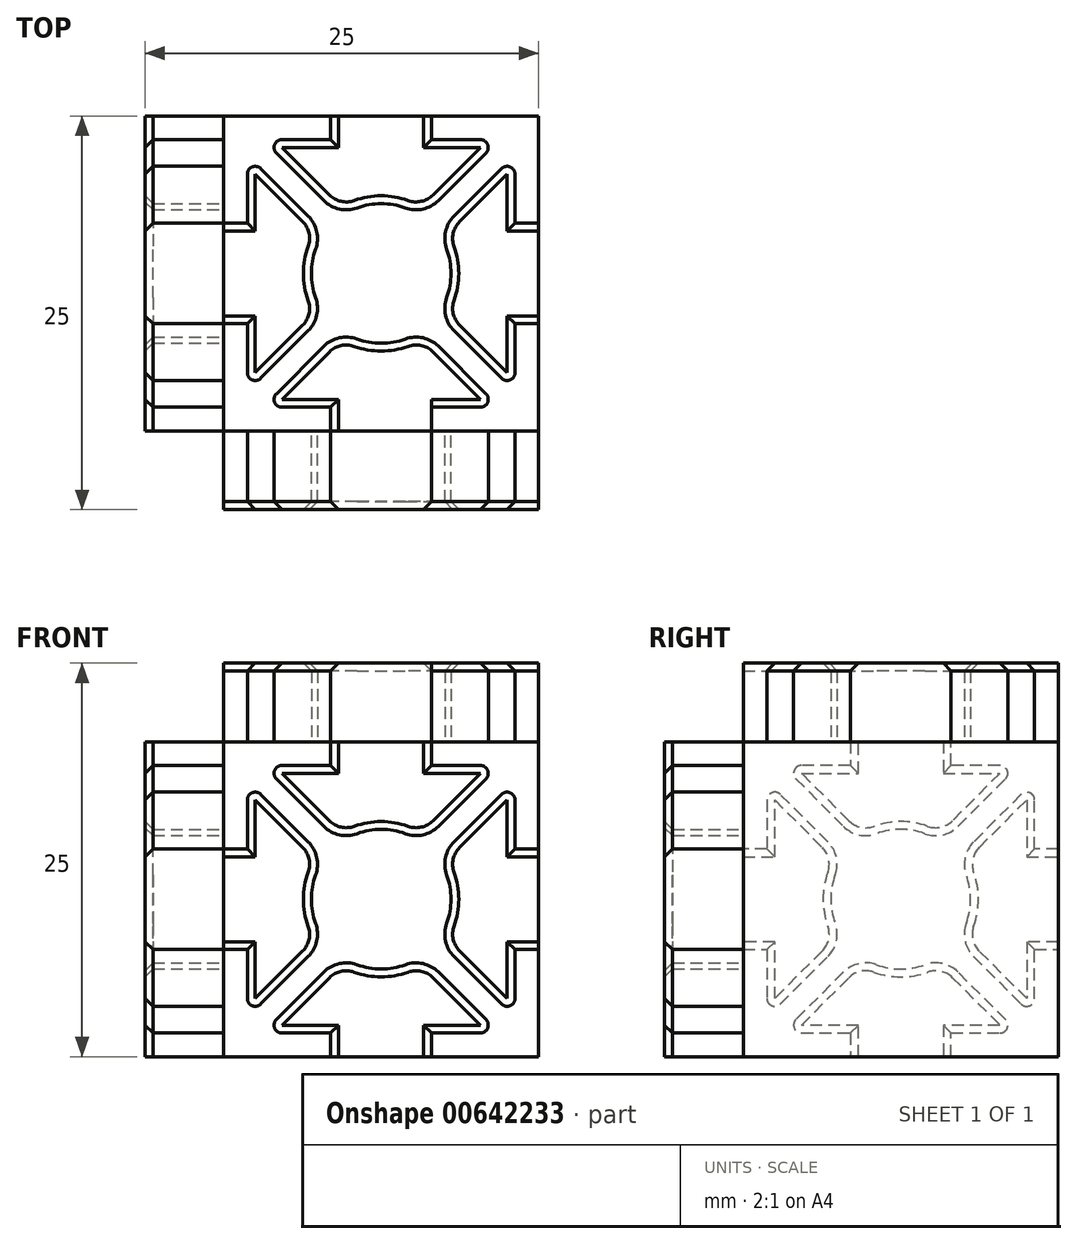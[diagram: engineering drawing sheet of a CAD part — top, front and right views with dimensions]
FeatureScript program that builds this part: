
annotation { "Feature Type Name" : "Feature", "Feature Type Description" : "" }
export const myFeature = defineFeature(function(context is Context, id is Id, definition is map)
    precondition{}
    {
        {
            var Q0;
            Q0=qCreatedBy(makeId("Top.planeOp"),FACE);
            var sketch = newSketch(context, id + "F0", { "sketchPlane" : qUnion([Q0])});
            skCircle(sketch, "E0", {"center": v(10, 10) * mm, "radius": 2.5 * mm});
            skLineSegment(sketch, "E1", {"start": v(0, 0) * mm, "end": v(10, 10) * mm, "construction": true});
            skLineSegment(sketch, "E2", {"start": v(1.5, 2.49) * mm, "end": v(1.5, 6.8) * mm});
            skLineSegment(sketch, "E3", {"start": v(1.5, 6.8) * mm, "end": v(0, 6.8) * mm});
            skLineSegment(sketch, "E4", {"start": v(0, 6.8) * mm, "end": v(0, 0) * mm});
            skLineSegment(sketch, "E5", {"start": v(7.39, 6.4) * mm, "end": v(2.49, 1.5) * mm});
            skLineSegment(sketch, "E6", {"start": v(2.49, 1.5) * mm, "end": v(6.8, 1.5) * mm});
            skLineSegment(sketch, "E7", {"start": v(6.8, 1.5) * mm, "end": v(6.8, 0) * mm});
            skLineSegment(sketch, "E8", {"start": v(6.8, 0) * mm, "end": v(0, 0) * mm});
            skLineSegment(sketch, "E9", {"start": v(10, 10) * mm, "end": v(20, 20) * mm, "construction": true});
            skLineSegment(sketch, "E10", {"start": v(10, 10) * mm, "end": v(0, 20) * mm, "construction": true});
            skLineSegment(sketch, "E11", {"start": v(10, 10) * mm, "end": v(20, 0) * mm, "construction": true});
            skLineSegment(sketch, "E12", {"start": v(1.5, 17.51) * mm, "end": v(6.4, 12.61) * mm});
            skLineSegment(sketch, "E13", {"start": v(1.5, 17.51) * mm, "end": v(1.5, 13.2) * mm});
            skLineSegment(sketch, "E14", {"start": v(1.5, 13.2) * mm, "end": v(0, 13.2) * mm});
            skLineSegment(sketch, "E15", {"start": v(0, 13.2) * mm, "end": v(0, 20) * mm});
            skLineSegment(sketch, "E16", {"start": v(7.39, 13.6) * mm, "end": v(2.49, 18.5) * mm});
            skLineSegment(sketch, "E17", {"start": v(2.49, 18.5) * mm, "end": v(6.8, 18.5) * mm});
            skLineSegment(sketch, "E18", {"start": v(6.8, 18.5) * mm, "end": v(6.8, 20) * mm});
            skLineSegment(sketch, "E19", {"start": v(6.8, 20) * mm, "end": v(0, 20) * mm});
            skLineSegment(sketch, "E20", {"start": v(12.61, 13.6) * mm, "end": v(17.51, 18.5) * mm});
            skLineSegment(sketch, "E21", {"start": v(17.51, 18.5) * mm, "end": v(13.2, 18.5) * mm});
            skLineSegment(sketch, "E22", {"start": v(13.2, 18.5) * mm, "end": v(13.2, 20) * mm});
            skLineSegment(sketch, "E23", {"start": v(13.2, 20) * mm, "end": v(20, 20) * mm});
            skLineSegment(sketch, "E24", {"start": v(13.6, 12.61) * mm, "end": v(18.5, 17.51) * mm});
            skLineSegment(sketch, "E25", {"start": v(18.5, 17.51) * mm, "end": v(18.5, 13.2) * mm});
            skLineSegment(sketch, "E26", {"start": v(18.5, 13.2) * mm, "end": v(20, 13.2) * mm});
            skLineSegment(sketch, "E27", {"start": v(20, 13.2) * mm, "end": v(20, 20) * mm});
            skLineSegment(sketch, "E28", {"start": v(18.5, 2.49) * mm, "end": v(18.5, 6.8) * mm});
            skLineSegment(sketch, "E29", {"start": v(18.5, 6.8) * mm, "end": v(20, 6.8) * mm});
            skLineSegment(sketch, "E30", {"start": v(20, 6.8) * mm, "end": v(20, 0) * mm});
            skLineSegment(sketch, "E31", {"start": v(12.61, 6.4) * mm, "end": v(17.51, 1.5) * mm});
            skLineSegment(sketch, "E32", {"start": v(17.51, 1.5) * mm, "end": v(13.2, 1.5) * mm});
            skLineSegment(sketch, "E33", {"start": v(13.2, 1.5) * mm, "end": v(13.2, 0) * mm});
            skLineSegment(sketch, "E34", {"start": v(13.2, 0) * mm, "end": v(20, 0) * mm});
            skLineSegment(sketch, "E35", {"start": v(10, 10) * mm, "end": v(10, 0) * mm, "construction": true});
            skLineSegment(sketch, "E36", {"start": v(10, 10) * mm, "end": v(18.77, 10) * mm, "construction": true});
            skLineSegment(sketch, "E37", {"start": v(10, 10) * mm, "end": v(10, 20.74) * mm, "construction": true});
            skLineSegment(sketch, "E38", {"start": v(10, 10) * mm, "end": v(0, 10) * mm, "construction": true});
            skLineSegment(sketch, "E39.bottom", {"start": v(0, 0) * mm, "end": v(20, 0) * mm, "construction": true});
            skLineSegment(sketch, "E39.top", {"start": v(0, 20) * mm, "end": v(20, 20) * mm, "construction": true});
            skLineSegment(sketch, "E39.left", {"start": v(0, 0) * mm, "end": v(0, 20) * mm, "construction": true});
            skLineSegment(sketch, "E39.right", {"start": v(20, 0) * mm, "end": v(20, 20) * mm, "construction": true});
            skLineSegment(sketch, "E40", {"start": v(18.5, 2.49) * mm, "end": v(13.6, 7.39) * mm});
            skLineSegment(sketch, "E41", {"start": v(1.5, 2.49) * mm, "end": v(6.4, 7.39) * mm});
            skLineSegment(sketch, "E42", {"start": v(20, 13.2) * mm, "end": v(20, 6.8) * mm});
            skLineSegment(sketch, "E43", {"start": v(6.8, 20) * mm, "end": v(13.2, 20) * mm});
            skLineSegment(sketch, "E44", {"start": v(0, 13.2) * mm, "end": v(0, 6.8) * mm});
            skLineSegment(sketch, "E45", {"start": v(6.8, 0) * mm, "end": v(13.2, 0) * mm});
            skArc(sketch, "E46", {"start": v(12.61, 13.6) * mm, "mid": v(10, 14.43) * mm, "end": v(7.39, 13.6) * mm});
            skArc(sketch, "E47", {"start": v(6.4, 12.61) * mm, "mid": v(5.57, 10) * mm, "end": v(6.4, 7.39) * mm});
            skArc(sketch, "E48", {"start": v(13.6, 7.39) * mm, "mid": v(14.43, 10) * mm, "end": v(13.6, 12.61) * mm});
            skArc(sketch, "E49", {"start": v(7.39, 6.4) * mm, "mid": v(10, 5.57) * mm, "end": v(12.61, 6.4) * mm});
            skSolve(sketch);
        }
        {
            var Q0;
            Q0=makeQuery(id+"F0.imprint","IMPRINT",FACE,{"disambiguationData":[TD([[makeQuery(id+"F0.imprint","IMPRINT",EDGE,{"derivedFrom":sQuery(id+"F0.wireOp",EDGE,"E16")}),-1.0]])]});
            var Q1;
            Q1=makeQuery(id+"F0.imprint","IMPRINT",FACE,{"disambiguationData":[TD([[makeQuery(id+"F0.imprint","IMPRINT",EDGE,{"derivedFrom":sQuery(id+"F0.wireOp",EDGE,"E24")}),-1.0]])]});
            var Q2;
            Q2=makeQuery(id+"F0.imprint","IMPRINT",FACE,{"disambiguationData":[TD([[makeQuery(id+"F0.imprint","IMPRINT",EDGE,{"derivedFrom":sQuery(id+"F0.wireOp",EDGE,"E5")}),1.0]])]});
            var Q3;
            Q3=makeQuery(id+"F0.imprint","IMPRINT",FACE,{"disambiguationData":[TD([[makeQuery(id+"F0.imprint","IMPRINT",EDGE,{"derivedFrom":sQuery(id+"F0.wireOp",EDGE,"E2")}),-1.0]])]});
            extrude(context, id + "F1", {"entities" : qUnion([Q0, Q1, Q2, Q3]), "depth" : 5 * mm, "offsetDistance" : 25 * mm});
        }
        {
            var Q0;
            Q0=qCreatedBy(makeId("Right.planeOp"),FACE);
            var sketch = newSketch(context, id + "F2", { "sketchPlane" : qUnion([Q0])});
            skCircle(sketch, "E50", {"center": v(10, -10) * mm, "radius": 2.5 * mm});
            skLineSegment(sketch, "E51", {"start": v(0, -20) * mm, "end": v(10, -10) * mm, "construction": true});
            skLineSegment(sketch, "E52", {"start": v(1.5, -17.51) * mm, "end": v(1.5, -13.2) * mm});
            skLineSegment(sketch, "E53", {"start": v(1.5, -13.2) * mm, "end": v(0, -13.2) * mm});
            skLineSegment(sketch, "E54", {"start": v(7.39, -13.6) * mm, "end": v(2.49, -18.5) * mm});
            skLineSegment(sketch, "E55", {"start": v(2.49, -18.5) * mm, "end": v(6.8, -18.5) * mm});
            skLineSegment(sketch, "E56", {"start": v(6.8, -18.5) * mm, "end": v(6.8, -20) * mm});
            skLineSegment(sketch, "E57", {"start": v(10, -10) * mm, "end": v(20, 0) * mm, "construction": true});
            skLineSegment(sketch, "E58", {"start": v(10, -10) * mm, "end": v(0, 0) * mm, "construction": true});
            skLineSegment(sketch, "E59", {"start": v(10, -10) * mm, "end": v(20, -20) * mm, "construction": true});
            skLineSegment(sketch, "E60", {"start": v(1.5, -2.49) * mm, "end": v(6.4, -7.39) * mm});
            skLineSegment(sketch, "E61", {"start": v(1.5, -2.49) * mm, "end": v(1.5, -6.8) * mm});
            skLineSegment(sketch, "E62", {"start": v(1.5, -6.8) * mm, "end": v(0, -6.8) * mm});
            skLineSegment(sketch, "E63", {"start": v(7.39, -6.4) * mm, "end": v(2.49, -1.5) * mm});
            skLineSegment(sketch, "E64", {"start": v(2.49, -1.5) * mm, "end": v(6.8, -1.5) * mm});
            skLineSegment(sketch, "E65", {"start": v(6.8, -1.5) * mm, "end": v(6.8, 0) * mm});
            skLineSegment(sketch, "E66", {"start": v(12.61, -6.4) * mm, "end": v(17.51, -1.5) * mm});
            skLineSegment(sketch, "E67", {"start": v(17.51, -1.5) * mm, "end": v(13.2, -1.5) * mm});
            skLineSegment(sketch, "E68", {"start": v(13.2, -1.5) * mm, "end": v(13.2, 0) * mm});
            skLineSegment(sketch, "E69", {"start": v(13.6, -7.39) * mm, "end": v(18.5, -2.49) * mm});
            skLineSegment(sketch, "E70", {"start": v(18.5, -2.49) * mm, "end": v(18.5, -6.8) * mm});
            skLineSegment(sketch, "E71", {"start": v(18.5, -6.8) * mm, "end": v(20, -6.8) * mm});
            skLineSegment(sketch, "E72", {"start": v(18.5, -17.51) * mm, "end": v(18.5, -13.2) * mm});
            skLineSegment(sketch, "E73", {"start": v(18.5, -13.2) * mm, "end": v(20, -13.2) * mm});
            skLineSegment(sketch, "E74", {"start": v(12.61, -13.6) * mm, "end": v(17.51, -18.5) * mm});
            skLineSegment(sketch, "E75", {"start": v(17.51, -18.5) * mm, "end": v(13.2, -18.5) * mm});
            skLineSegment(sketch, "E76", {"start": v(13.2, -18.5) * mm, "end": v(13.2, -20) * mm});
            skLineSegment(sketch, "E77", {"start": v(18.5, -17.51) * mm, "end": v(13.6, -12.61) * mm});
            skLineSegment(sketch, "E78", {"start": v(1.5, -17.51) * mm, "end": v(6.4, -12.61) * mm});
            skLineSegment(sketch, "E79", {"start": v(20, -6.8) * mm, "end": v(20, -13.2) * mm});
            skLineSegment(sketch, "E80", {"start": v(6.8, 0) * mm, "end": v(13.2, 0) * mm});
            skLineSegment(sketch, "E81", {"start": v(0, -6.8) * mm, "end": v(0, -13.2) * mm});
            skLineSegment(sketch, "E82", {"start": v(6.8, -20) * mm, "end": v(13.2, -20) * mm});
            skArc(sketch, "E83", {"start": v(12.61, -6.4) * mm, "mid": v(10, -5.57) * mm, "end": v(7.39, -6.4) * mm});
            skArc(sketch, "E84", {"start": v(6.4, -7.39) * mm, "mid": v(5.57, -10) * mm, "end": v(6.4, -12.61) * mm});
            skArc(sketch, "E85", {"start": v(13.6, -12.61) * mm, "mid": v(14.43, -10) * mm, "end": v(13.6, -7.39) * mm});
            skArc(sketch, "E86", {"start": v(7.39, -13.6) * mm, "mid": v(10, -14.43) * mm, "end": v(12.61, -13.6) * mm});
            skLineSegment(sketch, "E87.bottom", {"start": v(20, 0) * mm, "end": v(0, 0) * mm, "construction": true});
            skLineSegment(sketch, "E87.top", {"start": v(20, -20) * mm, "end": v(0, -20) * mm, "construction": true});
            skLineSegment(sketch, "E87.left", {"start": v(20, 0) * mm, "end": v(20, -20) * mm, "construction": true});
            skLineSegment(sketch, "E87.right", {"start": v(0, 0) * mm, "end": v(0, -20) * mm, "construction": true});
            skSolve(sketch);
        }
        {
            var Q0;
            Q0=makeQuery(id+"F2.imprint","IMPRINT",FACE,{"disambiguationData":[TD([[makeQuery(id+"F2.imprint","IMPRINT",EDGE,{"derivedFrom":sQuery(id+"F2.wireOp",EDGE,"E63")}),-1.0]])]});
            var Q1;
            Q1=makeQuery(id+"F2.imprint","IMPRINT",FACE,{"disambiguationData":[TD([[makeQuery(id+"F2.imprint","IMPRINT",EDGE,{"derivedFrom":sQuery(id+"F2.wireOp",EDGE,"E69")}),-1.0]])]});
            var Q2;
            Q2=makeQuery(id+"F2.imprint","IMPRINT",FACE,{"disambiguationData":[TD([[makeQuery(id+"F2.imprint","IMPRINT",EDGE,{"derivedFrom":sQuery(id+"F2.wireOp",EDGE,"E54")}),1.0]])]});
            var Q3;
            Q3=makeQuery(id+"F2.imprint","IMPRINT",FACE,{"disambiguationData":[TD([[makeQuery(id+"F2.imprint","IMPRINT",EDGE,{"derivedFrom":sQuery(id+"F2.wireOp",EDGE,"E52")}),-1.0]])]});
            extrude(context, id + "F3", {"entities" : qUnion([Q0, Q1, Q2, Q3]), "operationType" : NewBodyOperationType.ADD, "oppositeDirection" : true, "depth" : 5 * mm, "offsetDistance" : 25 * mm});
        }
        {
            var Q0;
            Q0=qCreatedBy(makeId("Front.planeOp"),FACE);
            var sketch = newSketch(context, id + "F4", { "sketchPlane" : qUnion([Q0])});
            skCircle(sketch, "E88", {"center": v(10, -10) * mm, "radius": 2.5 * mm});
            skLineSegment(sketch, "E89", {"start": v(0, -20) * mm, "end": v(10, -10) * mm, "construction": true});
            skLineSegment(sketch, "E90", {"start": v(1.5, -17.51) * mm, "end": v(1.5, -13.2) * mm});
            skLineSegment(sketch, "E91", {"start": v(1.5, -13.2) * mm, "end": v(0, -13.2) * mm});
            skLineSegment(sketch, "E92", {"start": v(7.39, -13.6) * mm, "end": v(2.49, -18.5) * mm});
            skLineSegment(sketch, "E93", {"start": v(2.49, -18.5) * mm, "end": v(6.8, -18.5) * mm});
            skLineSegment(sketch, "E94", {"start": v(6.8, -18.5) * mm, "end": v(6.8, -20) * mm});
            skLineSegment(sketch, "E95", {"start": v(10, -10) * mm, "end": v(20, 0) * mm, "construction": true});
            skLineSegment(sketch, "E96", {"start": v(10, -10) * mm, "end": v(0, 0) * mm, "construction": true});
            skLineSegment(sketch, "E97", {"start": v(10, -10) * mm, "end": v(20, -20) * mm, "construction": true});
            skLineSegment(sketch, "E98", {"start": v(1.5, -2.49) * mm, "end": v(6.4, -7.39) * mm});
            skLineSegment(sketch, "E99", {"start": v(1.5, -2.49) * mm, "end": v(1.5, -6.8) * mm});
            skLineSegment(sketch, "E100", {"start": v(1.5, -6.8) * mm, "end": v(0, -6.8) * mm});
            skLineSegment(sketch, "E101", {"start": v(7.39, -6.4) * mm, "end": v(2.49, -1.5) * mm});
            skLineSegment(sketch, "E102", {"start": v(2.49, -1.5) * mm, "end": v(6.8, -1.5) * mm});
            skLineSegment(sketch, "E103", {"start": v(6.8, -1.5) * mm, "end": v(6.8, 0) * mm});
            skLineSegment(sketch, "E104", {"start": v(12.61, -6.4) * mm, "end": v(17.51, -1.5) * mm});
            skLineSegment(sketch, "E105", {"start": v(17.51, -1.5) * mm, "end": v(13.2, -1.5) * mm});
            skLineSegment(sketch, "E106", {"start": v(13.2, -1.5) * mm, "end": v(13.2, 0) * mm});
            skLineSegment(sketch, "E107", {"start": v(13.6, -7.39) * mm, "end": v(18.5, -2.49) * mm});
            skLineSegment(sketch, "E108", {"start": v(18.5, -2.49) * mm, "end": v(18.5, -6.8) * mm});
            skLineSegment(sketch, "E109", {"start": v(18.5, -6.8) * mm, "end": v(20, -6.8) * mm});
            skLineSegment(sketch, "E110", {"start": v(18.5, -17.51) * mm, "end": v(18.5, -13.2) * mm});
            skLineSegment(sketch, "E111", {"start": v(18.5, -13.2) * mm, "end": v(20, -13.2) * mm});
            skLineSegment(sketch, "E112", {"start": v(12.61, -13.6) * mm, "end": v(17.51, -18.5) * mm});
            skLineSegment(sketch, "E113", {"start": v(17.51, -18.5) * mm, "end": v(13.2, -18.5) * mm});
            skLineSegment(sketch, "E114", {"start": v(13.2, -18.5) * mm, "end": v(13.2, -20) * mm});
            skLineSegment(sketch, "E115", {"start": v(18.5, -17.51) * mm, "end": v(13.6, -12.61) * mm});
            skLineSegment(sketch, "E116", {"start": v(1.5, -17.51) * mm, "end": v(6.4, -12.61) * mm});
            skLineSegment(sketch, "E117", {"start": v(20, -6.8) * mm, "end": v(20, -13.2) * mm});
            skLineSegment(sketch, "E118", {"start": v(6.8, 0) * mm, "end": v(13.2, 0) * mm});
            skLineSegment(sketch, "E119", {"start": v(0, -6.8) * mm, "end": v(0, -13.2) * mm});
            skLineSegment(sketch, "E120", {"start": v(6.8, -20) * mm, "end": v(13.2, -20) * mm});
            skArc(sketch, "E121", {"start": v(12.61, -6.4) * mm, "mid": v(10, -5.57) * mm, "end": v(7.39, -6.4) * mm});
            skArc(sketch, "E122", {"start": v(6.4, -7.39) * mm, "mid": v(5.57, -10) * mm, "end": v(6.4, -12.61) * mm});
            skArc(sketch, "E123", {"start": v(13.6, -12.61) * mm, "mid": v(14.43, -10) * mm, "end": v(13.6, -7.39) * mm});
            skArc(sketch, "E124", {"start": v(7.39, -13.6) * mm, "mid": v(10, -14.43) * mm, "end": v(12.61, -13.6) * mm});
            skLineSegment(sketch, "E125.bottom", {"start": v(0, 0) * mm, "end": v(20, 0) * mm, "construction": true});
            skLineSegment(sketch, "E125.top", {"start": v(0, -20) * mm, "end": v(20, -20) * mm, "construction": true});
            skLineSegment(sketch, "E125.left", {"start": v(0, 0) * mm, "end": v(0, -20) * mm, "construction": true});
            skLineSegment(sketch, "E125.right", {"start": v(20, 0) * mm, "end": v(20, -20) * mm, "construction": true});
            skSolve(sketch);
        }
        {
            var Q0;
            Q0=makeQuery(id+"F4.imprint","IMPRINT",FACE,{"disambiguationData":[TD([[makeQuery(id+"F4.imprint","IMPRINT",EDGE,{"derivedFrom":sQuery(id+"F4.wireOp",EDGE,"E101")}),-1.0]])]});
            var Q1;
            Q1=makeQuery(id+"F4.imprint","IMPRINT",FACE,{"disambiguationData":[TD([[makeQuery(id+"F4.imprint","IMPRINT",EDGE,{"derivedFrom":sQuery(id+"F4.wireOp",EDGE,"E107")}),-1.0]])]});
            var Q2;
            Q2=makeQuery(id+"F4.imprint","IMPRINT",FACE,{"disambiguationData":[TD([[makeQuery(id+"F4.imprint","IMPRINT",EDGE,{"derivedFrom":sQuery(id+"F4.wireOp",EDGE,"E92")}),1.0]])]});
            var Q3;
            Q3=makeQuery(id+"F4.imprint","IMPRINT",FACE,{"disambiguationData":[TD([[makeQuery(id+"F4.imprint","IMPRINT",EDGE,{"derivedFrom":sQuery(id+"F4.wireOp",EDGE,"E90")}),-1.0]])]});
            extrude(context, id + "F5", {"entities" : qUnion([Q0, Q1, Q2, Q3]), "operationType" : NewBodyOperationType.ADD, "depth" : 5 * mm, "offsetDistance" : 25 * mm});
        }
        {
            var Q0;
            Q0=makeQuery(id+"F0.imprint","IMPRINT",FACE,{"disambiguationData":[TD([[makeQuery(id+"F0.imprint","IMPRINT",EDGE,{"derivedFrom":sQuery(id+"F0.wireOp",EDGE,"E0")}),-1.0]])]});
            var sketch = newSketch(context, id + "F6", { "sketchPlane" : qUnion([Q0])});
            skLineSegment(sketch, "E126.bottom", {"start": v(0, 0) * mm, "end": v(20, 0) * mm});
            skLineSegment(sketch, "E126.top", {"start": v(0, 20) * mm, "end": v(20, 20) * mm});
            skLineSegment(sketch, "E126.left", {"start": v(0, 0) * mm, "end": v(0, 20) * mm});
            skLineSegment(sketch, "E126.right", {"start": v(20, 0) * mm, "end": v(20, 20) * mm});
            skSolve(sketch);
        }
        {
            var Q0;
            Q0=makeQuery(id+"F6.imprint","IMPRINT",FACE,{"disambiguationData":[TD([[makeQuery(id+"F6.imprint","IMPRINT",EDGE,{"derivedFrom":makeQuery(id+"F0.imprint","IMPRINT",EDGE,{"derivedFrom":sQuery(id+"F0.wireOp",EDGE,"E0")})}),-1.0]])]});
            var Q1;
            Q1=makeQuery(id+"F6.imprint","IMPRINT",FACE,{"disambiguationData":[TD([[makeQuery(id+"F6.imprint","IMPRINT",EDGE,{"derivedFrom":makeQuery(id+"F0.imprint","IMPRINT",EDGE,{"derivedFrom":sQuery(id+"F0.wireOp",EDGE,"E24")})}),-1.0]])]});
            var Q2;
            Q2=makeQuery(id+"F6.imprint","IMPRINT",FACE,{"disambiguationData":[TD([[makeQuery(id+"F6.imprint","IMPRINT",EDGE,{"derivedFrom":makeQuery(id+"F0.imprint","IMPRINT",EDGE,{"derivedFrom":sQuery(id+"F0.wireOp",EDGE,"E16")})}),-1.0]])]});
            var Q3;
            Q3=makeQuery(id+"F6.imprint","IMPRINT",FACE,{"disambiguationData":[TD([[makeQuery(id+"F6.imprint","IMPRINT",EDGE,{"derivedFrom":makeQuery(id+"F0.imprint","IMPRINT",EDGE,{"derivedFrom":sQuery(id+"F0.wireOp",EDGE,"E2")})}),-1.0]])]});
            var Q4;
            Q4=makeQuery(id+"F6.imprint","IMPRINT",FACE,{"disambiguationData":[TD([[makeQuery(id+"F6.imprint","IMPRINT",EDGE,{"derivedFrom":makeQuery(id+"F0.imprint","IMPRINT",EDGE,{"derivedFrom":sQuery(id+"F0.wireOp",EDGE,"E5")})}),1.0]])]});
            var Q5;
            Q5=makeQuery(id+"F6.imprint","IMPRINT",FACE,{"disambiguationData":[TD([[makeQuery(id+"F6.imprint","IMPRINT",EDGE,{"derivedFrom":makeQuery(id+"F0.imprint","IMPRINT",EDGE,{"derivedFrom":sQuery(id+"F0.wireOp",EDGE,"E0")})}),1.0]])]});
            extrude(context, id + "F7", {"entities" : qUnion([Q0, Q1, Q2, Q3, Q4, Q5]), "oppositeDirection" : true, "depth" : 20 * mm, "offsetDistance" : 25 * mm});
        }
        {
            var Q0;
            Q0=makeQuery(id+"F5.opExtrude","SWEPT_EDGE",EDGE,{"disambiguationData":[OSD([sQuery(id+"F4.wireOp",EDGE,"E107"),sQuery(id+"F4.wireOp",EDGE,"E108")])]});
            var Q1;
            Q1=makeQuery(id+"F5.opExtrude","SWEPT_EDGE",EDGE,{"disambiguationData":[OSD([sQuery(id+"F4.wireOp",EDGE,"E104"),sQuery(id+"F4.wireOp",EDGE,"E105")])]});
            var Q2;
            Q2=makeQuery(id+"F5.opExtrude","SWEPT_EDGE",EDGE,{"disambiguationData":[OSD([sQuery(id+"F4.wireOp",EDGE,"E110"),sQuery(id+"F4.wireOp",EDGE,"E115")])]});
            var Q3;
            Q3=makeQuery(id+"F5.opExtrude","SWEPT_EDGE",EDGE,{"disambiguationData":[OSD([sQuery(id+"F4.wireOp",EDGE,"E112"),sQuery(id+"F4.wireOp",EDGE,"E113")])]});
            var Q4;
            Q4=makeQuery(id+"F5.opExtrude","SWEPT_EDGE",EDGE,{"disambiguationData":[OSD([sQuery(id+"F4.wireOp",EDGE,"E92"),sQuery(id+"F4.wireOp",EDGE,"E93")])]});
            var Q5;
            Q5=makeQuery(id+"F5.opExtrude","SWEPT_EDGE",EDGE,{"disambiguationData":[OSD([sQuery(id+"F4.wireOp",EDGE,"E90"),sQuery(id+"F4.wireOp",EDGE,"E116")])]});
            var Q6;
            Q6=makeQuery(id+"F5.opExtrude","SWEPT_EDGE",EDGE,{"disambiguationData":[OSD([sQuery(id+"F4.wireOp",EDGE,"E98"),sQuery(id+"F4.wireOp",EDGE,"E99")])]});
            var Q7;
            Q7=makeQuery(id+"F5.opExtrude","SWEPT_EDGE",EDGE,{"disambiguationData":[OSD([sQuery(id+"F4.wireOp",EDGE,"E101"),sQuery(id+"F4.wireOp",EDGE,"E102")])]});
            var Q8;
            Q8=makeQuery(id+"F1.opExtrude","SWEPT_EDGE",EDGE,{"disambiguationData":[OSD([sQuery(id+"F0.wireOp",EDGE,"E5"),sQuery(id+"F0.wireOp",EDGE,"E6")])]});
            var Q9;
            Q9=makeQuery(id+"F1.opExtrude","SWEPT_EDGE",EDGE,{"disambiguationData":[OSD([sQuery(id+"F0.wireOp",EDGE,"E2"),sQuery(id+"F0.wireOp",EDGE,"E41")])]});
            var Q10;
            Q10=makeQuery(id+"F1.opExtrude","SWEPT_EDGE",EDGE,{"disambiguationData":[OSD([sQuery(id+"F0.wireOp",EDGE,"E31"),sQuery(id+"F0.wireOp",EDGE,"E32")])]});
            var Q11;
            Q11=makeQuery(id+"F1.opExtrude","SWEPT_EDGE",EDGE,{"disambiguationData":[OSD([sQuery(id+"F0.wireOp",EDGE,"E28"),sQuery(id+"F0.wireOp",EDGE,"E40")])]});
            var Q12;
            Q12=makeQuery(id+"F1.opExtrude","SWEPT_EDGE",EDGE,{"disambiguationData":[OSD([sQuery(id+"F0.wireOp",EDGE,"E24"),sQuery(id+"F0.wireOp",EDGE,"E25")])]});
            var Q13;
            Q13=makeQuery(id+"F1.opExtrude","SWEPT_EDGE",EDGE,{"disambiguationData":[OSD([sQuery(id+"F0.wireOp",EDGE,"E20"),sQuery(id+"F0.wireOp",EDGE,"E21")])]});
            var Q14;
            Q14=makeQuery(id+"F1.opExtrude","SWEPT_EDGE",EDGE,{"disambiguationData":[OSD([sQuery(id+"F0.wireOp",EDGE,"E16"),sQuery(id+"F0.wireOp",EDGE,"E17")])]});
            var Q15;
            Q15=makeQuery(id+"F1.opExtrude","SWEPT_EDGE",EDGE,{"disambiguationData":[OSD([sQuery(id+"F0.wireOp",EDGE,"E12"),sQuery(id+"F0.wireOp",EDGE,"E13")])]});
            var Q16;
            Q16=makeQuery(id+"F3.opExtrude","SWEPT_EDGE",EDGE,{"disambiguationData":[OSD([sQuery(id+"F2.wireOp",EDGE,"E66"),sQuery(id+"F2.wireOp",EDGE,"E67")])]});
            var Q17;
            Q17=makeQuery(id+"F3.opExtrude","SWEPT_EDGE",EDGE,{"disambiguationData":[OSD([sQuery(id+"F2.wireOp",EDGE,"E69"),sQuery(id+"F2.wireOp",EDGE,"E70")])]});
            var Q18;
            Q18=makeQuery(id+"F3.opExtrude","SWEPT_EDGE",EDGE,{"disambiguationData":[OSD([sQuery(id+"F2.wireOp",EDGE,"E63"),sQuery(id+"F2.wireOp",EDGE,"E64")])]});
            var Q19;
            Q19=makeQuery(id+"F3.opExtrude","SWEPT_EDGE",EDGE,{"disambiguationData":[OSD([sQuery(id+"F2.wireOp",EDGE,"E60"),sQuery(id+"F2.wireOp",EDGE,"E61")])]});
            var Q20;
            Q20=makeQuery(id+"F3.opExtrude","SWEPT_EDGE",EDGE,{"disambiguationData":[OSD([sQuery(id+"F2.wireOp",EDGE,"E52"),sQuery(id+"F2.wireOp",EDGE,"E78")])]});
            var Q21;
            Q21=makeQuery(id+"F3.opExtrude","SWEPT_EDGE",EDGE,{"disambiguationData":[OSD([sQuery(id+"F2.wireOp",EDGE,"E54"),sQuery(id+"F2.wireOp",EDGE,"E55")])]});
            var Q22;
            Q22=makeQuery(id+"F3.opExtrude","SWEPT_EDGE",EDGE,{"disambiguationData":[OSD([sQuery(id+"F2.wireOp",EDGE,"E74"),sQuery(id+"F2.wireOp",EDGE,"E75")])]});
            var Q23;
            Q23=makeQuery(id+"F3.opExtrude","SWEPT_EDGE",EDGE,{"disambiguationData":[OSD([sQuery(id+"F2.wireOp",EDGE,"E72"),sQuery(id+"F2.wireOp",EDGE,"E77")])]});
            fillet(context, id + "F8", {"entities" : qUnion([Q0, Q1, Q2, Q3, Q4, Q5, Q6, Q7, Q8, Q9, Q10, Q11, Q12, Q13, Q14, Q15, Q16, Q17, Q18, Q19, Q20, Q21, Q22, Q23]), "radius" : 0.5 * mm, "tangentPropagation" : true, "allowEdgeOverflow" : false});
        }
        {
            var Q0;
            Q0=makeQuery(id+"F3.opExtrude","SWEPT_EDGE",EDGE,{"disambiguationData":[OSD([sQuery(id+"F2.wireOp",EDGE,"E69"),sQuery(id+"F2.wireOp",EDGE,"E85")])]});
            var Q1;
            Q1=makeQuery(id+"F3.opExtrude","SWEPT_EDGE",EDGE,{"disambiguationData":[OSD([sQuery(id+"F2.wireOp",EDGE,"E77"),sQuery(id+"F2.wireOp",EDGE,"E85")])]});
            var Q2;
            Q2=makeQuery(id+"F3.opExtrude","SWEPT_EDGE",EDGE,{"disambiguationData":[OSD([sQuery(id+"F2.wireOp",EDGE,"E66"),sQuery(id+"F2.wireOp",EDGE,"E83")])]});
            var Q3;
            Q3=makeQuery(id+"F3.opExtrude","SWEPT_EDGE",EDGE,{"disambiguationData":[OSD([sQuery(id+"F2.wireOp",EDGE,"E63"),sQuery(id+"F2.wireOp",EDGE,"E83")])]});
            var Q4;
            Q4=makeQuery(id+"F3.opExtrude","SWEPT_EDGE",EDGE,{"disambiguationData":[OSD([sQuery(id+"F2.wireOp",EDGE,"E78"),sQuery(id+"F2.wireOp",EDGE,"E84")])]});
            var Q5;
            Q5=makeQuery(id+"F3.opExtrude","SWEPT_EDGE",EDGE,{"disambiguationData":[OSD([sQuery(id+"F2.wireOp",EDGE,"E60"),sQuery(id+"F2.wireOp",EDGE,"E84")])]});
            var Q6;
            Q6=makeQuery(id+"F3.opExtrude","SWEPT_EDGE",EDGE,{"disambiguationData":[OSD([sQuery(id+"F2.wireOp",EDGE,"E74"),sQuery(id+"F2.wireOp",EDGE,"E86")])]});
            var Q7;
            Q7=makeQuery(id+"F3.opExtrude","SWEPT_EDGE",EDGE,{"disambiguationData":[OSD([sQuery(id+"F2.wireOp",EDGE,"E54"),sQuery(id+"F2.wireOp",EDGE,"E86")])]});
            var Q8;
            Q8=makeQuery(id+"F5.opExtrude","SWEPT_EDGE",EDGE,{"disambiguationData":[OSD([sQuery(id+"F4.wireOp",EDGE,"E98"),sQuery(id+"F4.wireOp",EDGE,"E122")])]});
            var Q9;
            Q9=makeQuery(id+"F5.opExtrude","SWEPT_EDGE",EDGE,{"disambiguationData":[OSD([sQuery(id+"F4.wireOp",EDGE,"E116"),sQuery(id+"F4.wireOp",EDGE,"E122")])]});
            var Q10;
            Q10=makeQuery(id+"F5.opExtrude","SWEPT_EDGE",EDGE,{"disambiguationData":[OSD([sQuery(id+"F4.wireOp",EDGE,"E92"),sQuery(id+"F4.wireOp",EDGE,"E124")])]});
            var Q11;
            Q11=makeQuery(id+"F5.opExtrude","SWEPT_EDGE",EDGE,{"disambiguationData":[OSD([sQuery(id+"F4.wireOp",EDGE,"E112"),sQuery(id+"F4.wireOp",EDGE,"E124")])]});
            var Q12;
            Q12=makeQuery(id+"F5.opExtrude","SWEPT_EDGE",EDGE,{"disambiguationData":[OSD([sQuery(id+"F4.wireOp",EDGE,"E115"),sQuery(id+"F4.wireOp",EDGE,"E123")])]});
            var Q13;
            Q13=makeQuery(id+"F5.opExtrude","SWEPT_EDGE",EDGE,{"disambiguationData":[OSD([sQuery(id+"F4.wireOp",EDGE,"E101"),sQuery(id+"F4.wireOp",EDGE,"E121")])]});
            var Q14;
            Q14=makeQuery(id+"F5.opExtrude","SWEPT_EDGE",EDGE,{"disambiguationData":[OSD([sQuery(id+"F4.wireOp",EDGE,"E104"),sQuery(id+"F4.wireOp",EDGE,"E121")])]});
            var Q15;
            Q15=makeQuery(id+"F5.opExtrude","SWEPT_EDGE",EDGE,{"disambiguationData":[OSD([sQuery(id+"F4.wireOp",EDGE,"E107"),sQuery(id+"F4.wireOp",EDGE,"E123")])]});
            var Q16;
            Q16=makeQuery(id+"F1.opExtrude","SWEPT_EDGE",EDGE,{"disambiguationData":[OSD([sQuery(id+"F0.wireOp",EDGE,"E12"),sQuery(id+"F0.wireOp",EDGE,"E47")])]});
            var Q17;
            Q17=makeQuery(id+"F1.opExtrude","SWEPT_EDGE",EDGE,{"disambiguationData":[OSD([sQuery(id+"F0.wireOp",EDGE,"E41"),sQuery(id+"F0.wireOp",EDGE,"E47")])]});
            var Q18;
            Q18=makeQuery(id+"F1.opExtrude","SWEPT_EDGE",EDGE,{"disambiguationData":[OSD([sQuery(id+"F0.wireOp",EDGE,"E5"),sQuery(id+"F0.wireOp",EDGE,"E49")])]});
            var Q19;
            Q19=makeQuery(id+"F1.opExtrude","SWEPT_EDGE",EDGE,{"disambiguationData":[OSD([sQuery(id+"F0.wireOp",EDGE,"E40"),sQuery(id+"F0.wireOp",EDGE,"E48")])]});
            var Q20;
            Q20=makeQuery(id+"F1.opExtrude","SWEPT_EDGE",EDGE,{"disambiguationData":[OSD([sQuery(id+"F0.wireOp",EDGE,"E31"),sQuery(id+"F0.wireOp",EDGE,"E49")])]});
            var Q21;
            Q21=makeQuery(id+"F1.opExtrude","SWEPT_EDGE",EDGE,{"disambiguationData":[OSD([sQuery(id+"F0.wireOp",EDGE,"E20"),sQuery(id+"F0.wireOp",EDGE,"E46")])]});
            var Q22;
            Q22=makeQuery(id+"F1.opExtrude","SWEPT_EDGE",EDGE,{"disambiguationData":[OSD([sQuery(id+"F0.wireOp",EDGE,"E16"),sQuery(id+"F0.wireOp",EDGE,"E46")])]});
            var Q23;
            Q23=makeQuery(id+"F1.opExtrude","SWEPT_EDGE",EDGE,{"disambiguationData":[OSD([sQuery(id+"F0.wireOp",EDGE,"E24"),sQuery(id+"F0.wireOp",EDGE,"E48")])]});
            fillet(context, id + "F9", {"entities" : qUnion([Q0, Q1, Q2, Q3, Q4, Q5, Q6, Q7, Q8, Q9, Q10, Q11, Q12, Q13, Q14, Q15, Q16, Q17, Q18, Q19, Q20, Q21, Q22, Q23]), "radius" : 2 * mm, "tangentPropagation" : true, "allowEdgeOverflow" : false});
        }
        {
            var Q0;
            Q0=makeQuery(id+"F5.opExtrude","CAP_EDGE",EDGE,{"disambiguationData":[OSD([sQuery(id+"F4.wireOp",EDGE,"E104")])],"isStart":false});
            var Q1;
            Q1=makeQuery(id+"F5.opExtrude","CAP_EDGE",EDGE,{"disambiguationData":[OSD([sQuery(id+"F4.wireOp",EDGE,"E106")])],"isStart":false});
            var Q2;
            Q2=makeQuery(id+"F5.opExtrude","CAP_EDGE",EDGE,{"disambiguationData":[OSD([sQuery(id+"F4.wireOp",EDGE,"E103")])],"isStart":false});
            var Q3;
            {var subQ0=sQuery(id+"F4.wireOp",EDGE,"E123");var subQ1=sQuery(id+"F4.wireOp",EDGE,"E107");Q3=makeQuery(id+"F9.opFillet","BLEND_EDGE",EDGE,{"blendedFrom":[makeQuery(id+"F5.opExtrude","SWEPT_EDGE",EDGE,{"disambiguationData":[OSD([subQ1,subQ0])]}),makeQuery(id+"F5.opExtrude","CAP_FACE",FACE,{"disambiguationData":[OSD([subQ1,sQuery(id+"F4.wireOp",EDGE,"E108"),sQuery(id+"F4.wireOp",EDGE,"E109"),sQuery(id+"F4.wireOp",EDGE,"E110"),sQuery(id+"F4.wireOp",EDGE,"E111"),sQuery(id+"F4.wireOp",EDGE,"E115"),sQuery(id+"F4.wireOp",EDGE,"E117"),subQ0])],"isStart":false})],"blendedInto":[makeQuery(id+"F5.opExtrude","CAP_FACE",FACE,{"disambiguationData":[OSD([subQ1,sQuery(id+"F4.wireOp",EDGE,"E108"),sQuery(id+"F4.wireOp",EDGE,"E109"),sQuery(id+"F4.wireOp",EDGE,"E110"),sQuery(id+"F4.wireOp",EDGE,"E111"),sQuery(id+"F4.wireOp",EDGE,"E115"),sQuery(id+"F4.wireOp",EDGE,"E117"),subQ0])],"isStart":false})]});}
            var Q4;
            Q4=makeQuery(id+"F5.opExtrude","CAP_EDGE",EDGE,{"disambiguationData":[OSD([sQuery(id+"F4.wireOp",EDGE,"E124")])],"isStart":false});
            var Q5;
            Q5=makeQuery(id+"F5.opExtrude","CAP_EDGE",EDGE,{"disambiguationData":[OSD([sQuery(id+"F4.wireOp",EDGE,"E94")])],"isStart":false});
            var Q6;
            Q6=makeQuery(id+"F5.opExtrude","CAP_EDGE",EDGE,{"disambiguationData":[OSD([sQuery(id+"F4.wireOp",EDGE,"E114")])],"isStart":false});
            var Q7;
            Q7=makeQuery(id+"F5.opExtrude","CAP_EDGE",EDGE,{"disambiguationData":[OSD([sQuery(id+"F4.wireOp",EDGE,"E111")])],"isStart":false});
            var Q8;
            Q8=makeQuery(id+"F5.opExtrude","CAP_EDGE",EDGE,{"disambiguationData":[OSD([sQuery(id+"F4.wireOp",EDGE,"E109")])],"isStart":false});
            var Q9;
            Q9=makeQuery(id+"F5.opExtrude","CAP_EDGE",EDGE,{"disambiguationData":[OSD([sQuery(id+"F4.wireOp",EDGE,"E122")])],"isStart":false});
            var Q10;
            Q10=makeQuery(id+"F5.opExtrude","CAP_EDGE",EDGE,{"disambiguationData":[OSD([sQuery(id+"F4.wireOp",EDGE,"E100")])],"isStart":false});
            var Q11;
            Q11=makeQuery(id+"F5.opExtrude","CAP_EDGE",EDGE,{"disambiguationData":[OSD([sQuery(id+"F4.wireOp",EDGE,"E91")])],"isStart":false});
            var Q12;
            Q12=makeQuery(id+"F1.opExtrude","CAP_EDGE",EDGE,{"disambiguationData":[OSD([sQuery(id+"F0.wireOp",EDGE,"E41")])],"isStart":false});
            var Q13;
            Q13=makeQuery(id+"F1.opExtrude","CAP_EDGE",EDGE,{"disambiguationData":[OSD([sQuery(id+"F0.wireOp",EDGE,"E46")])],"isStart":false});
            var Q14;
            Q14=makeQuery(id+"F1.opExtrude","CAP_EDGE",EDGE,{"disambiguationData":[OSD([sQuery(id+"F0.wireOp",EDGE,"E48")])],"isStart":false});
            var Q15;
            Q15=makeQuery(id+"F1.opExtrude","CAP_EDGE",EDGE,{"disambiguationData":[OSD([sQuery(id+"F0.wireOp",EDGE,"E49")])],"isStart":false});
            var Q16;
            Q16=makeQuery(id+"F1.opExtrude","CAP_EDGE",EDGE,{"disambiguationData":[OSD([sQuery(id+"F0.wireOp",EDGE,"E29")])],"isStart":false});
            var Q17;
            Q17=makeQuery(id+"F1.opExtrude","CAP_EDGE",EDGE,{"disambiguationData":[OSD([sQuery(id+"F0.wireOp",EDGE,"E3")])],"isStart":false});
            var Q18;
            Q18=makeQuery(id+"F1.opExtrude","CAP_EDGE",EDGE,{"disambiguationData":[OSD([sQuery(id+"F0.wireOp",EDGE,"E22")])],"isStart":false});
            var Q19;
            Q19=makeQuery(id+"F1.opExtrude","CAP_EDGE",EDGE,{"disambiguationData":[OSD([sQuery(id+"F0.wireOp",EDGE,"E18")])],"isStart":false});
            var Q20;
            Q20=makeQuery(id+"F1.opExtrude","CAP_EDGE",EDGE,{"disambiguationData":[OSD([sQuery(id+"F0.wireOp",EDGE,"E7")])],"isStart":false});
            var Q21;
            Q21=makeQuery(id+"F1.opExtrude","CAP_EDGE",EDGE,{"disambiguationData":[OSD([sQuery(id+"F0.wireOp",EDGE,"E14")])],"isStart":false});
            var Q22;
            Q22=makeQuery(id+"F3.opExtrude","CAP_EDGE",EDGE,{"disambiguationData":[OSD([sQuery(id+"F2.wireOp",EDGE,"E86")])],"isStart":false});
            var Q23;
            Q23=makeQuery(id+"F3.opExtrude","CAP_EDGE",EDGE,{"disambiguationData":[OSD([sQuery(id+"F2.wireOp",EDGE,"E85")])],"isStart":false});
            var Q24;
            Q24=makeQuery(id+"F3.opExtrude","CAP_EDGE",EDGE,{"disambiguationData":[OSD([sQuery(id+"F2.wireOp",EDGE,"E83")])],"isStart":false});
            var Q25;
            Q25=makeQuery(id+"F3.opExtrude","CAP_EDGE",EDGE,{"disambiguationData":[OSD([sQuery(id+"F2.wireOp",EDGE,"E84")])],"isStart":false});
            var Q26;
            Q26=makeQuery(id+"F3.opExtrude","CAP_EDGE",EDGE,{"disambiguationData":[OSD([sQuery(id+"F2.wireOp",EDGE,"E73")])],"isStart":false});
            var Q27;
            Q27=makeQuery(id+"F3.opExtrude","CAP_EDGE",EDGE,{"disambiguationData":[OSD([sQuery(id+"F2.wireOp",EDGE,"E76")])],"isStart":false});
            var Q28;
            Q28=makeQuery(id+"F3.opExtrude","CAP_EDGE",EDGE,{"disambiguationData":[OSD([sQuery(id+"F2.wireOp",EDGE,"E53")])],"isStart":false});
            var Q29;
            Q29=makeQuery(id+"F3.opExtrude","CAP_EDGE",EDGE,{"disambiguationData":[OSD([sQuery(id+"F2.wireOp",EDGE,"E68")])],"isStart":false});
            var Q30;
            Q30=makeQuery(id+"F3.opExtrude","CAP_EDGE",EDGE,{"disambiguationData":[OSD([sQuery(id+"F2.wireOp",EDGE,"E65")])],"isStart":false});
            var Q31;
            Q31=makeQuery(id+"F3.opExtrude","CAP_EDGE",EDGE,{"disambiguationData":[OSD([sQuery(id+"F2.wireOp",EDGE,"E56")])],"isStart":false});
            var Q32;
            Q32=makeQuery(id+"F3.opExtrude","CAP_EDGE",EDGE,{"disambiguationData":[OSD([sQuery(id+"F2.wireOp",EDGE,"E62")])],"isStart":false});
            var Q33;
            Q33=makeQuery(id+"F3.opExtrude","CAP_EDGE",EDGE,{"disambiguationData":[OSD([sQuery(id+"F2.wireOp",EDGE,"E71")])],"isStart":false});
            var Q34;
            Q34=makeQuery(id+"F1.opExtrude","CAP_EDGE",EDGE,{"disambiguationData":[OSD([sQuery(id+"F0.wireOp",EDGE,"E26")])],"isStart":false});
            chamfer(context, id + "F10", {"entities" : qUnion([Q0, Q1, Q2, Q3, Q4, Q5, Q6, Q7, Q8, Q9, Q10, Q11, Q12, Q13, Q14, Q15, Q16, Q17, Q18, Q19, Q20, Q21, Q22, Q23, Q24, Q25, Q26, Q27, Q28, Q29, Q30, Q31, Q32, Q33, Q34]), "width" : 0.5 * mm, "tangentPropagation" : true});
        }
    });
